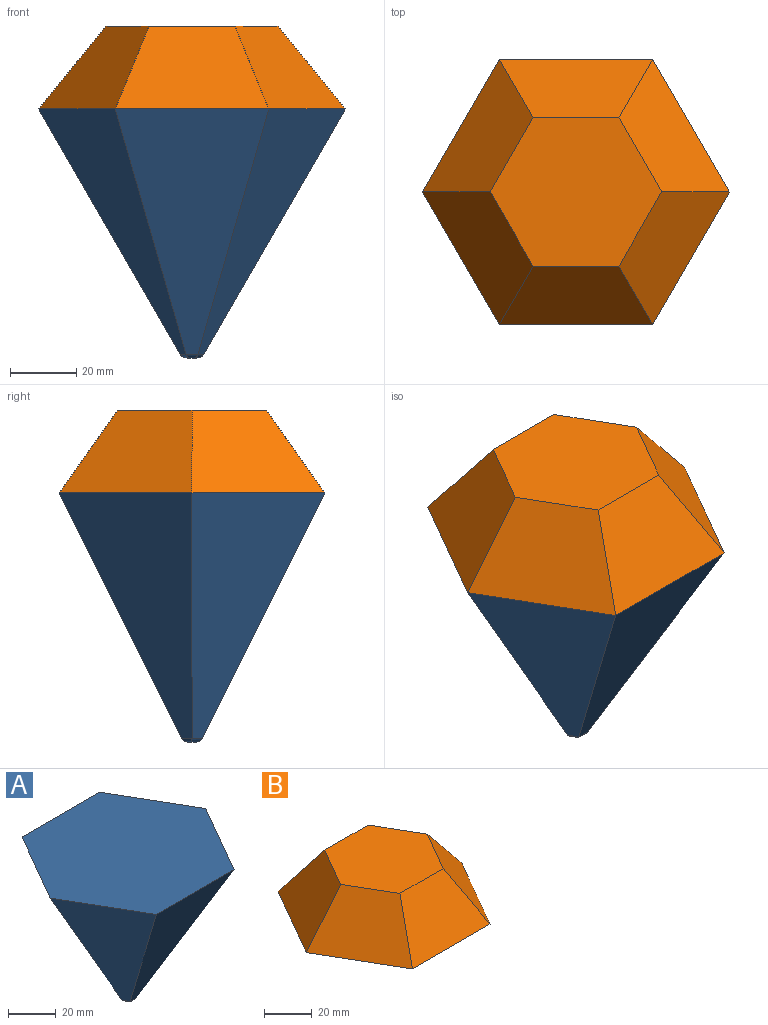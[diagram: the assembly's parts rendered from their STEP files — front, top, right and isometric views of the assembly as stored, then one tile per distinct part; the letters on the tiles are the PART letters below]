
ASSEMBLY  parts=2 mates=1
PART A: 14 faces, bbox 92.4x80x75 mm
  f0: plane 73.89x44.43mm, normal (0.77,0.45,-0.45), area 2053.6mm2, adj f1,f5,f6,f13
  f1: plane 73.89x44.43mm, normal (0.77,-0.45,-0.45), area 2053.6mm2, adj f0,f2,f6,f11
  f2: plane 73.89x46.19mm, normal (0,-0.89,-0.45), area 2053.6mm2, adj f1,f3,f6,f9
  f3: plane 73.89x44.43mm, normal (-0.77,-0.45,-0.45), area 2053.6mm2, adj f2,f4,f6,f8
  f4: plane 73.89x44.43mm, normal (-0.77,0.45,-0.45), area 2053.6mm2, adj f3,f5,f6,f10
  f5: plane 73.89x46.19mm, normal (0,0.89,-0.45), area 2053.6mm2, adj f0,f4,f6,f12
  f6: plane 92.38x80mm, normal (0,0,1), area 5542.6mm2, adj f0,f1,f2,f3,f4,f5
  f7: plane 2.92x2.53mm, normal (0,0,-1), area 5.5mm2, adj f8,f9,f10,f11,f12,f13
  f8: cylinder r=2mm len=3.95mm, axis (0.5,-0.87,0), area 5.8mm2, adj f3,f7,f9,f10
  f9: cylinder r=2mm len=3.53mm, axis (1,0,0), area 5.8mm2, adj f2,f7,f8,f11
  f10: cylinder r=2mm len=3.95mm, axis (-0.5,-0.87,0), area 5.8mm2, adj f4,f7,f8,f12
  f11: cylinder r=2mm len=3.95mm, axis (0.5,0.87,0), area 5.8mm2, adj f1,f7,f9,f13
  f12: cylinder r=2mm len=3.53mm, axis (-1,0,0), area 5.8mm2, adj f5,f7,f10,f13
  f13: cylinder r=2mm len=3.95mm, axis (-0.5,0.87,0), area 5.8mm2, adj f0,f7,f11,f12
PART B: 8 faces, bbox 92.4x80x25 mm
  f0: plane 92.38x80mm, normal (0,0,-1), area 5542.6mm2, adj f2,f3,f4,f5,f6,f7
  f1: plane 51.63x44.71mm, normal (0,0,1), area 1731.5mm2, adj f2,f3,f4,f5,f6,f7
  f2: plane 46.19x25mm, normal (0,0.82,0.58), area 1101.6mm2, adj f0,f1,f3,f7
  f3: plane 40x33.28mm, normal (-0.71,0.41,0.58), area 1101.6mm2, adj f0,f1,f2,f4
  f4: plane 40x33.28mm, normal (-0.71,-0.41,0.58), area 1101.6mm2, adj f0,f1,f3,f5
  f5: plane 46.19x25mm, normal (0,-0.82,0.58), area 1101.6mm2, adj f0,f1,f4,f6
  f6: plane 40x33.28mm, normal (0.71,-0.41,0.58), area 1101.6mm2, adj f0,f1,f5,f7
  f7: plane 40x33.28mm, normal (0.71,0.41,0.58), area 1101.6mm2, adj f0,f1,f2,f6
PLACE A at identity fixed
PLACE B t=(0,0,-5)mm
MATE fastened B.f0 <-> A.f6  axis (0,0,-1) through (0,0,-5)mm
